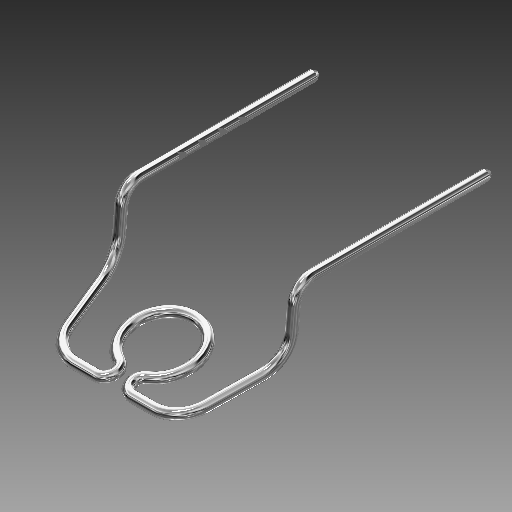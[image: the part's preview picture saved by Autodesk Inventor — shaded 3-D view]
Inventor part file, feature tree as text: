
AUTODESK INVENTOR PART (.ipt)
format: ipt  version: 2019 (Build 230136000, 136)  size: 248,832 bytes
history: native  units: mm
features: sketch x7, plane x4, sweep x3, other x3, chamfer x2, projected_geometry x2, mirror x1, extrude x1
ambient origin geometry x8: Origin, YZ Plane, XZ Plane, XY Plane, X Axis, Y Axis, Z Axis, Center Point
bodies: Solid1 (feature_tree)
feature tree (23):
  plane  "Work Plane1"
  sketch  "Sketch2"  dims[d0=85.0mm d1=175.0mm]
  plane  "Work Plane2"
  sweep  "Sweep1"
  plane  "Work Plane3"
  sweep  "Sweep2"
  other  "Work Axis2"
  mirror  "Mirror1"
  plane  "Work Plane4"
  sweep  "Sweep3"
  chamfer  "Chamfer1"  Distance=46.0mm
  chamfer  "Chamfer2"  [1 undecoded]
  extrude  "Extrusion1"  Depth=30.0mm
  sketch  "Sketch3"  dims[d2=17.5mm d3=21.0mm]
  other  "Work Axis1"
  sketch  "Sketch4"  dims[d5=16.580628mm d6=10.0mm]
  sketch  "Sketch5"  dims[d7=0.0mm]
  other  "Work Axis3"
  sketch  "Sketch6"  dims[d8=15.0deg]
  sketch  "Sketch7"  dims[d9=33.0mm]
  sketch  "Sketch8"  dims[d10=18.849556mm d11=46.0mm d12=0.0mm d13=30.0mm d15=10.0mm d17=65.0mm d19=18.0mm d20=0.0mm d21=4.0mm d22=2.0mm d23=30.0deg d24=4.0mm d25=2.0mm d26=30.0deg d27=2.5mm d29=12.217305mm d30=140.0mm d31=40.0mm d33=20.0mm d34=10.0mm d36=10.0mm d38=10.0mm d39=0.0mm d40=0.0mm d41=0.0mm d42=0.0mm]
  projected_geometry  "Projected Loop1"
  projected_geometry  "Projected Loop2"
note: 1 required parameter value undecoded (feature->parameter linkage not recoverable at this tier; creation-order binding heuristic only, values carry confidence <= 0.55)
